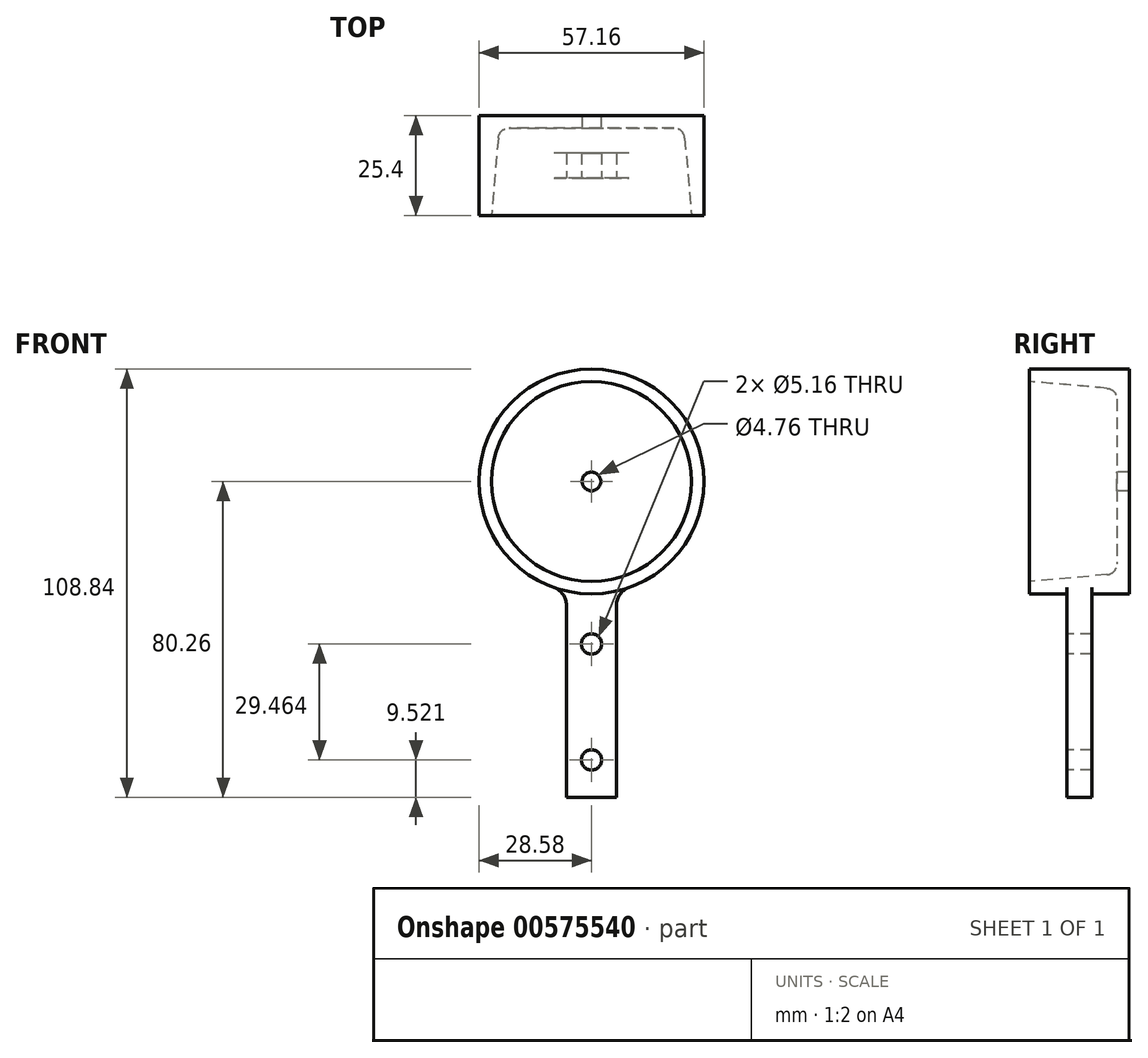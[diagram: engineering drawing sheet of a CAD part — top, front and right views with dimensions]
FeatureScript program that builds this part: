
annotation { "Feature Type Name" : "Feature", "Feature Type Description" : "" }
export const myFeature = defineFeature(function(context is Context, id is Id, definition is map)
    precondition{}
    {
        {
            var Q0;
            Q0=qCreatedBy(makeId("Front.planeOp"),FACE);
            var sketch = newSketch(context, id + "F0", { "sketchPlane" : qUnion([Q0])});
            skArc(sketch, "E0", {"start": v(9.53, -26.94) * mm, "mid": v(0, 28.57) * mm, "end": v(-9.52, -26.94) * mm});
            skLineSegment(sketch, "E1", {"start": v(6.35, -31.43) * mm, "end": v(6.35, -80.26) * mm});
            skLineSegment(sketch, "E2", {"start": v(6.35, -80.26) * mm, "end": v(-6.35, -80.26) * mm});
            skLineSegment(sketch, "E3", {"start": v(-6.35, -80.26) * mm, "end": v(-6.35, -31.43) * mm});
            skPoint(sketch, "E4.visualSharp", {"position": v(-6.35, -27.86) * mm});
            skArc(sketch, "E4.filletArc", {"start": v(-6.35, -31.43) * mm, "mid": v(-7.22, -28.68) * mm, "end": v(-9.53, -26.94) * mm});
            skPoint(sketch, "E5.visualSharp", {"position": v(6.35, -27.86) * mm});
            skArc(sketch, "E5.filletArc", {"start": v(9.53, -26.94) * mm, "mid": v(7.22, -28.68) * mm, "end": v(6.35, -31.43) * mm});
            skCircle(sketch, "E6", {"center": v(0, -41.28) * mm, "radius": 2.58 * mm});
            skCircle(sketch, "E7", {"center": v(0, -70.74) * mm, "radius": 2.58 * mm});
            skCircle(sketch, "E8", {"center": v(0, 0) * mm, "radius": 28.58 * mm, "construction": true});
            skPoint(sketch, "E9", {"position": v(0, 28.58) * mm});
            skPoint(sketch, "E10", {"position": v(0, -28.58) * mm});
            skCircle(sketch, "E11", {"center": v(0, 0) * mm, "radius": 2.38 * mm});
            skSolve(sketch);
        }
        {
            var Q0;
            Q0=qCreatedBy(makeId("Right.planeOp"),FACE);
            var sketch = newSketch(context, id + "F1", { "sketchPlane" : qUnion([Q0])});
            skLineSegment(sketch, "E12", {"start": v(0, 0) * mm, "end": v(25.4, 0) * mm, "construction": true});
            skLineSegment(sketch, "E13", {"start": v(0, 25.4) * mm, "end": v(19.69, 23.68) * mm});
            skLineSegment(sketch, "E14", {"start": v(22.22, 20.9) * mm, "end": v(22.23, 0) * mm});
            skPoint(sketch, "E15.visualSharp", {"position": v(22.22, 23.46) * mm});
            skArc(sketch, "E15.filletArc", {"start": v(22.22, 20.9) * mm, "mid": v(21.5, 22.79) * mm, "end": v(19.69, 23.68) * mm});
            skLineSegment(sketch, "E16", {"start": v(0, 25.4) * mm, "end": v(0, 0) * mm});
            skLineSegment(sketch, "E17", {"start": v(22.23, 0) * mm, "end": v(0, 0) * mm});
            skPoint(sketch, "E18", {"position": v(19.69, 23.68) * mm});
            skLineSegment(sketch, "E19", {"start": v(19.69, 23.68) * mm, "end": v(19.45, 20.9) * mm});
            skSolve(sketch);
        }
        {
            var Q0;
            Q0=makeQuery(id+"F0.imprint","IMPRINT",FACE,{"disambiguationData":[TD([[makeQuery(id+"F0.imprint","IMPRINT",EDGE,{"derivedFrom":sQuery(id+"F0.wireOp",EDGE,"E0")}),1.0]])]});
            extrude(context, id + "F2", {"entities" : qUnion([Q0]), "oppositeDirection" : true, "depth" : 25.4 * mm, "offsetDistance" : 25.4 * mm});
        }
        {
            var Q0;
            Q0 = qSketchRegion(id + "F1", true);
            var Q1;
            Q1 = qConstructionFilter(qBodyType(qCreatedBy(id + "F1" ,EDGE), BodyType.WIRE), ConstructionObject.NO);
            var Q2;
            Q2=sQuery(id+"F1.wireOp",EDGE,"E12");
            revolve(context, id + "F3", {"operationType" : NewBodyOperationType.REMOVE, "entities" : qUnion([Q0]), "surfaceEntities" : qUnion([Q1]), "axis" : qUnion([Q2]), "revolveType" : RevolveType.FULL, "oppositeDirection" : true});
        }
        {
            var Q0;
            Q0=makeQuery(id+"F2.opExtrude","CAP_FACE",FACE,{"disambiguationData":[OSD([sQuery(id+"F0.wireOp",EDGE,"E0"),sQuery(id+"F0.wireOp",EDGE,"E1"),sQuery(id+"F0.wireOp",EDGE,"E2"),sQuery(id+"F0.wireOp",EDGE,"E3"),sQuery(id+"F0.wireOp",EDGE,"E4.filletArc"),sQuery(id+"F0.wireOp",EDGE,"E5.filletArc"),sQuery(id+"F0.wireOp",EDGE,"E6"),sQuery(id+"F0.wireOp",EDGE,"E7")])],"isStart":true});
            var sketch = newSketch(context, id + "F4", { "sketchPlane" : qUnion([Q0])});
            skArc(sketch, "E20", {"start": v(-9.52, -26.94) * mm, "mid": v(0, -28.57) * mm, "end": v(9.53, -26.94) * mm});
            skLineSegment(sketch, "E21", {"start": v(6.35, -80.26) * mm, "end": v(6.35, -31.43) * mm});
            skLineSegment(sketch, "E22", {"start": v(6.35, -80.26) * mm, "end": v(-6.35, -80.26) * mm});
            skLineSegment(sketch, "E23", {"start": v(-6.35, -80.26) * mm, "end": v(-6.35, -31.43) * mm});
            skArc(sketch, "E24.0", {"start": v(-6.35, -31.43) * mm, "mid": v(-7.22, -28.68) * mm, "end": v(-9.52, -26.94) * mm});
            skArc(sketch, "E25.0", {"start": v(9.53, -26.94) * mm, "mid": v(7.22, -28.68) * mm, "end": v(6.35, -31.43) * mm});
            skSolve(sketch);
        }
        {
            var Q0;
            Q0=makeQuery(id+"F4.imprint","IMPRINT",FACE,{"disambiguationData":[TD([[makeQuery(id+"F4.imprint","IMPRINT",EDGE,{"derivedFrom":sQuery(id+"F4.wireOp",EDGE,"E20")}),-1.0]])]});
            extrude(context, id + "F5", {"entities" : qUnion([Q0]), "operationType" : NewBodyOperationType.REMOVE, "oppositeDirection" : true, "depth" : 9.52 * mm, "offsetDistance" : 25.4 * mm});
        }
        {
            var Q0;
            Q0=makeQuery(id+"F2.opExtrude","CAP_FACE",FACE,{"disambiguationData":[OSD([sQuery(id+"F0.wireOp",EDGE,"E0"),sQuery(id+"F0.wireOp",EDGE,"E1"),sQuery(id+"F0.wireOp",EDGE,"E2"),sQuery(id+"F0.wireOp",EDGE,"E3"),sQuery(id+"F0.wireOp",EDGE,"E4.filletArc"),sQuery(id+"F0.wireOp",EDGE,"E5.filletArc"),sQuery(id+"F0.wireOp",EDGE,"E6"),sQuery(id+"F0.wireOp",EDGE,"E7")])],"isStart":false});
            var sketch = newSketch(context, id + "F6", { "sketchPlane" : qUnion([Q0])});
            skArc(sketch, "E26", {"start": v(-9.53, -26.94) * mm, "mid": v(0, -28.57) * mm, "end": v(9.52, -26.94) * mm});
            skLineSegment(sketch, "E27", {"start": v(-6.35, -80.26) * mm, "end": v(-6.35, -31.43) * mm});
            skLineSegment(sketch, "E28", {"start": v(-6.35, -80.26) * mm, "end": v(6.35, -80.26) * mm});
            skLineSegment(sketch, "E29", {"start": v(6.35, -80.26) * mm, "end": v(6.35, -31.43) * mm});
            skPoint(sketch, "E29.endSnap0", {"position": v(6.35, -55.85) * mm});
            skPoint(sketch, "E30.orphan", {"position": v(6.35, -15.98) * mm});
            skArc(sketch, "E31.0", {"start": v(-9.53, -26.94) * mm, "mid": v(-7.22, -28.68) * mm, "end": v(-6.35, -31.43) * mm});
            skArc(sketch, "E32.0", {"start": v(6.35, -31.43) * mm, "mid": v(7.22, -28.68) * mm, "end": v(9.52, -26.94) * mm});
            skSolve(sketch);
        }
        {
            var Q0;
            Q0=makeQuery(id+"F6.imprint","IMPRINT",FACE,{"disambiguationData":[TD([[makeQuery(id+"F6.imprint","IMPRINT",EDGE,{"derivedFrom":sQuery(id+"F6.wireOp",EDGE,"E26")}),-1.0]])]});
            extrude(context, id + "F7", {"entities" : qUnion([Q0]), "operationType" : NewBodyOperationType.REMOVE, "oppositeDirection" : true, "depth" : 9.52 * mm, "offsetDistance" : 25.4 * mm});
        }
    });
